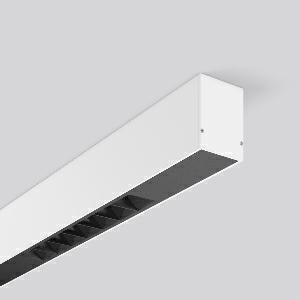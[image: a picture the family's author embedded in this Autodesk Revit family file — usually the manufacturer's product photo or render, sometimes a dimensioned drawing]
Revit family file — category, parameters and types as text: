
# Revit family: less_is_more_beamline_312500_002_e203
name_source: partatom
category: Lighting Fixtures
units: mm (PartAtom-declared; Revit-internal decimal feet)

## family parameters
Cut with Voids When Loaded = No
Host = Face
Light Source = No
Part Type = Normal
Room Calculation Point = No
Round Connector Dimension = Use Diameter
Shared = No

## types (1)
- LESS IS MORE BEAMLINE (1 x LED Modul 930, 1812.5 lm, 3000)
    Apparent Load = 97 VA
    CIE Flux Codes = 100 100 100 100 100
    Color Rendering = 90
    Color Temperature = 3000
    Default Elevation = 1800 mm
    Description = Series: LESS IS MORE BEAMLINE
Linear ceiling and wall luminaire for aesthetically sophisticated lighting. Luminaire with four LED light units. Housing: extruded aluminium profile, powder-coated. End cap aluminium powder-coated. LED light unit with MRS technology: Mini-Reflector-System made of metallised thermoplastic with prismatic black glare-suppressing frame for pleasant glare-free light (RUG < 10). Each LED light unit has 7 reflector elements. Wide beam light distribution. LED unit with integrated converter interchangeable and removable. Suitable for through-wiring. 
Colour: traffic white, matt (RAL 9016)
Length: 2248 mm
Width: 57 mm
Height: 75 mm
Lamp: LED
Socket: without socket
Colour temperature: 3000K
Colour rendering index (CRI): 90
System power: 97 W
Rated luminous flux: 7250 lm
Luminous efficiency: 75 lm/W
Control gear: Regulated power supply
Protection class: I
Type of protection: IP 20
    Height = 75 mm
    Lamp = 1 x LED Modul 930
    Lamp Light Flux = 1812.5 lm
    Lamp count = 1
    Length = 2248 mm
    Lifetime = 50000 h
    Luminous efficacy = 75 lm/W
    Manufacturer = RZB
    ModVariant = No
    Model = 312500.002
    Mounting Place = Ceiling, Wall
    Mounting Type = Surface mounted
    Number of Poles = 1
    OnlyDefault = Yes
    Power Factor = 1
    Product Name = LESS IS MORE BEAMLINE
    Product group = Surface mounted LED linear luminaires
    ProductGroupID = 307
    Protection Class = Protection class I
    Protection Degree = IP 20
    RLX_Detail_Level = 1
    RLX_Emergency_Light_Flux = 0 lm
    RLX_Emergency_Type = 0
    RLX_Emergency_Type_DB = No
    RlxData = <blob elided: 27461 chars, md5=2f31a9df>
    Socket = socket
    Standby Power = 0 W
    System Light Flux = 7250 lm
    System Power = 97 W
    Type Comments = Product without accessories
    Type Image = 312483.002.jpg
    URL = http://relux.com
    VarID = ---
    Voltage = 230 V
    Voltage Range = 220-240 V
    Weight = 0.00 kg
    Width = 57 mm

## geometry (parser evidence)
native form markers: Blend x4, Sweep x19
no freeform markers — native parametric forms only
